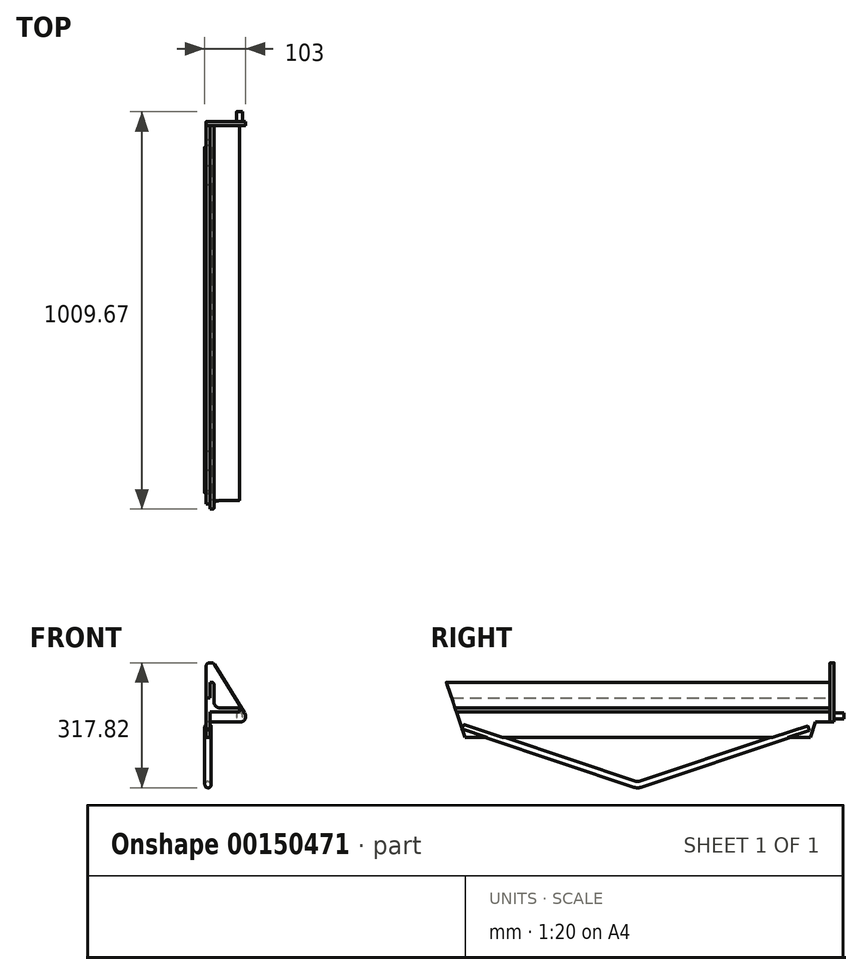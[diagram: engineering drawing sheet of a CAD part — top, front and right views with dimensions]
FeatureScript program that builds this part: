
annotation { "Feature Type Name" : "Feature", "Feature Type Description" : "" }
export const myFeature = defineFeature(function(context is Context, id is Id, definition is map)
    precondition{}
    {
        {
            var Q0;
            Q0=qCreatedBy(makeId("Front.planeOp"),FACE);
            var sketch = newSketch(context, id + "F0", { "sketchPlane" : qUnion([Q0])});
            skLineSegment(sketch, "E0", {"start": v(0, 75) * mm, "end": v(0, 0) * mm});
            skLineSegment(sketch, "E1", {"start": v(0, 0) * mm, "end": v(75, 0) * mm});
            skLineSegment(sketch, "E2", {"start": v(0, 75) * mm, "end": v(5, 75) * mm});
            skLineSegment(sketch, "E3", {"start": v(10, 70) * mm, "end": v(10, 26) * mm});
            skLineSegment(sketch, "E4", {"start": v(26, 10) * mm, "end": v(70, 10) * mm});
            skLineSegment(sketch, "E5", {"start": v(75, 5) * mm, "end": v(75, 0) * mm});
            skPoint(sketch, "E6.visualSharp", {"position": v(10, 10) * mm});
            skArc(sketch, "E6.filletArc", {"start": v(10, 26) * mm, "mid": v(14.69, 14.69) * mm, "end": v(26, 10) * mm});
            skPoint(sketch, "E7.visualSharp", {"position": v(10, 75) * mm});
            skArc(sketch, "E7.filletArc", {"start": v(10, 70) * mm, "mid": v(8.54, 73.54) * mm, "end": v(5, 75) * mm});
            skPoint(sketch, "E8.visualSharp", {"position": v(75, 10) * mm});
            skArc(sketch, "E8.filletArc", {"start": v(75, 5) * mm, "mid": v(73.54, 8.54) * mm, "end": v(70, 10) * mm});
            skSolve(sketch);
        }
        {
            var Q0;
            Q0=makeQuery(id+"F0.imprint","IMPRINT",FACE,{"disambiguationData":[TD([[makeQuery(id+"F0.imprint","IMPRINT",EDGE,{"derivedFrom":sQuery(id+"F0.wireOp",EDGE,"E0")}),1.0]])]});
            extrude(context, id + "F1", {"entities" : qUnion([Q0]), "depth" : 489 * mm, "hasSecondDirection" : true, "secondDirectionOppositeDirection" : true, "secondDirectionDepth" : 489 * mm});
        }
        {
            var Q0;
            Q0=qCreatedBy(makeId("Front.planeOp"),FACE);
            var sketch = newSketch(context, id + "F2", { "sketchPlane" : qUnion([Q0])});
            skLineSegment(sketch, "E9.bottom", {"start": v(0, 35) * mm, "end": v(-10, 35) * mm});
            skLineSegment(sketch, "E9.top", {"start": v(0, -65) * mm, "end": v(-10, -65) * mm});
            skLineSegment(sketch, "E9.left", {"start": v(0, 35) * mm, "end": v(0, -65) * mm});
            skLineSegment(sketch, "E9.right", {"start": v(-10, 35) * mm, "end": v(-10, -65) * mm});
            skSolve(sketch);
        }
        {
            var Q0;
            Q0=makeQuery(id+"F2.imprint","IMPRINT",FACE,{"disambiguationData":[TD([[makeQuery(id+"F2.imprint","IMPRINT",EDGE,{"derivedFrom":sQuery(id+"F2.wireOp",EDGE,"5NroJfMc-e3D6-tdf7-pEij-eTBKpccjXv2T.bottom")}),-1.0]])]});
            var Q1;
            Q1=makeQuery(id+"F2.imprint","IMPRINT",FACE,{"disambiguationData":[TD([[makeQuery(id+"F2.imprint","IMPRINT",EDGE,{"derivedFrom":sQuery(id+"F2.wireOp",EDGE,"E9.bottom")}),1.0]])]});
            extrude(context, id + "F3", {"entities" : qUnion([Q0, Q1]), "operationType" : NewBodyOperationType.ADD, "depth" : 489 * mm, "hasSecondDirection" : true, "secondDirectionOppositeDirection" : true, "secondDirectionDepth" : 489 * mm});
        }
        {
            var Q0;
            Q0=makeQuery(id+"F3.boolean.opBoolean","MERGE",FACE,{"derivedFrom":[makeQuery(id+"F1.opExtrude","CAP_FACE",FACE,{"disambiguationData":[OSD([sQuery(id+"F0.wireOp",EDGE,"E0"),sQuery(id+"F0.wireOp",EDGE,"E1"),sQuery(id+"F0.wireOp",EDGE,"E2"),sQuery(id+"F0.wireOp",EDGE,"E3"),sQuery(id+"F0.wireOp",EDGE,"E4"),sQuery(id+"F0.wireOp",EDGE,"E5"),sQuery(id+"F0.wireOp",EDGE,"E6.filletArc"),sQuery(id+"F0.wireOp",EDGE,"E7.filletArc"),sQuery(id+"F0.wireOp",EDGE,"E8.filletArc")])],"isStart":true}),makeQuery(id+"F3.opExtrude","CAP_FACE",FACE,{"disambiguationData":[OSD([sQuery(id+"F2.wireOp",EDGE,"5NroJfMc-e3D6-tdf7-pEij-eTBKpccjXv2T.bottom"),sQuery(id+"F2.wireOp",EDGE,"5NroJfMc-e3D6-tdf7-pEij-eTBKpccjXv2T.top"),sQuery(id+"F2.wireOp",EDGE,"5NroJfMc-e3D6-tdf7-pEij-eTBKpccjXv2T.left"),sQuery(id+"F2.wireOp",EDGE,"5NroJfMc-e3D6-tdf7-pEij-eTBKpccjXv2T.right")])],"isStart":true})]});
            var sketch = newSketch(context, id + "F4", { "sketchPlane" : qUnion([Q0])});
            skLineSegment(sketch, "E10.bottom", {"start": v(10, -25) * mm, "end": v(-90, -25) * mm});
            skLineSegment(sketch, "E10.top", {"start": v(10, 125) * mm, "end": v(-8.54, 125) * mm});
            skLineSegment(sketch, "E10.left", {"start": v(10, -25) * mm, "end": v(10, 125) * mm});
            skLineSegment(sketch, "E10.right", {"start": v(-90, -25) * mm, "end": v(-90, -5) * mm});
            skLineSegment(sketch, "E11", {"start": v(-8.54, 125) * mm, "end": v(-90, -5) * mm});
            skPoint(sketch, "E11.startSnap0", {"position": v(-8.54, 73.54) * mm});
            skSolve(sketch);
        }
        {
            var Q0;
            Q0 = qSketchRegion(id + "F4", true);
            extrude(context, id + "F5", {"entities" : qUnion([Q0]), "operationType" : NewBodyOperationType.ADD, "depth" : 10 * mm});
        }
        {
            var Q0;
            Q0=makeQuery(id+"F5.opExtrude","SWEPT_EDGE",EDGE,{"disambiguationData":[OSD([sQuery(id+"F4.wireOp",EDGE,"E10.top"),sQuery(id+"F4.wireOp",EDGE,"E11")])]});
            var Q1;
            Q1=makeQuery(id+"F5.opExtrude","SWEPT_EDGE",EDGE,{"disambiguationData":[OSD([sQuery(id+"F4.wireOp",EDGE,"E10.right"),sQuery(id+"F4.wireOp",EDGE,"E11")])]});
            var Q2;
            Q2=makeQuery(id+"F5.opExtrude","SWEPT_EDGE",EDGE,{"disambiguationData":[OSD([sQuery(id+"F4.wireOp",EDGE,"E10.bottom"),sQuery(id+"F4.wireOp",EDGE,"E10.right")])]});
            var Q3;
            Q3=makeQuery(id+"F5.opExtrude","SWEPT_EDGE",EDGE,{"disambiguationData":[OSD([sQuery(id+"F4.wireOp",EDGE,"E10.top"),sQuery(id+"F4.wireOp",EDGE,"E10.left")])]});
            fillet(context, id + "F6", {"entities" : qUnion([Q0, Q1, Q2, Q3]), "radius" : 10 * mm, "tangentPropagation" : true, "allowEdgeOverflow" : false});
        }
        {
            var Q0;
            Q0=makeQuery(id+"F5.opExtrude","CAP_FACE",FACE,{"disambiguationData":[OSD([sQuery(id+"F4.wireOp",EDGE,"E10.bottom"),sQuery(id+"F4.wireOp",EDGE,"E10.top"),sQuery(id+"F4.wireOp",EDGE,"E10.left"),sQuery(id+"F4.wireOp",EDGE,"E10.right"),sQuery(id+"F4.wireOp",EDGE,"E11")])],"isStart":false});
            var sketch = newSketch(context, id + "F7", { "sketchPlane" : qUnion([Q0])});
            skCircle(sketch, "E12", {"center": v(-75, -10) * mm, "radius": 8 * mm});
            skSolve(sketch);
        }
        {
            var Q0;
            Q0=makeQuery(id+"F7.imprint","IMPRINT",FACE,{"disambiguationData":[TD([[makeQuery(id+"F7.imprint","IMPRINT",EDGE,{"derivedFrom":sQuery(id+"F7.wireOp",EDGE,"E12")}),1.0]])]});
            extrude(context, id + "F8", {"entities" : qUnion([Q0]), "operationType" : NewBodyOperationType.ADD, "depth" : 25 * mm});
        }
        {
            var Q0;
            Q0=makeQuery(id+"F3.opExtrude","CAP_EDGE",EDGE,{"disambiguationData":[OSD([sQuery(id+"F2.wireOp",EDGE,"E9.top")])],"isStart":false});
            var Q1;
            Q1=makeQuery(id+"F3.opExtrude","CAP_EDGE",EDGE,{"disambiguationData":[OSD([sQuery(id+"F2.wireOp",EDGE,"E9.top")])],"isStart":true});
            chamfer(context, id + "F9", {"entities" : qUnion([Q0, Q1]), "chamferType" : ChamferType.TWO_OFFSETS, "width1" : 150 * mm, "oppositeDirection" : false, "width2" : 50 * mm, "tangentPropagation" : true});
        }
        {
            var Q0;
            {var subQ0=sQuery(id+"F4.wireOp",EDGE,"E10.left");Q0=makeQuery(id+"FGluRxbnb6SE4h9_1.1.F5.boolean.opBoolean","MERGE",FACE,{"derivedFrom":[makeQuery(id+"F5.boolean.opBoolean","MERGE",FACE,{"derivedFrom":[makeQuery(id+"F3.opExtrude","SWEPT_FACE",FACE,{"disambiguationData":[OSD([sQuery(id+"F2.wireOp",EDGE,"E9.right")])]}),makeQuery(id+"F5.opExtrude","SWEPT_FACE",FACE,{"disambiguationData":[OSD([subQ0])]})]}),makeQuery(id+"FGluRxbnb6SE4h9_1.1.F5.opExtrude","SWEPT_FACE",FACE,{"disambiguationData":[OSD([subQ0])]})]});}
            cPlane(context, id + "F10", {"entities" : qUnion([Q0]), "cplaneType" : CPlaneType.OFFSET, "offset" : 5 * mm, "oppositeDirection" : true, "width" : 150 * mm, "height" : 150 * mm});
        }
        {
            var Q0;
            Q0=qCreatedBy(id+"F10.planeOp",FACE);
            var sketch = newSketch(context, id + "F11", { "sketchPlane" : qUnion([Q0])});
            skLineSegment(sketch, "E13", {"start": v(444.1, -37.88) * mm, "end": v(6.32, -183.8) * mm});
            skLineSegment(sketch, "E14", {"start": v(-6.32, -183.8) * mm, "end": v(-434.51, -41.07) * mm});
            skPoint(sketch, "E15.visualSharp", {"position": v(0, -185.9) * mm});
            skArc(sketch, "E15.filletArc", {"start": v(-6.32, -183.8) * mm, "mid": v(0, -184.82) * mm, "end": v(6.32, -183.8) * mm});
            skSolve(sketch);
        }
        {
            var Q0;
            Q0=sQuery(id+"F11.wireOp",EDGE,"E14");
            var Q1;
            Q1=sQuery(id+"F11.wireOp",VERTEX,"E14.end");
            cPlane(context, id + "F12", {"entities" : qUnion([Q0, Q1]), "cplaneType" : CPlaneType.CURVE_POINT, "offset" : 25 * mm, "width" : 150 * mm, "height" : 150 * mm});
        }
        {
            var Q0;
            Q0=qCreatedBy(id+"F12.planeOp",FACE);
            var sketch = newSketch(context, id + "F13", { "sketchPlane" : qUnion([Q0])});
            skCircle(sketch, "E16", {"center": v(5, -176.37) * mm, "radius": 8 * mm});
            skSolve(sketch);
        }
        {
            var Q0;
            Q0=makeQuery(id+"F13.imprint","IMPRINT",FACE,{"disambiguationData":[TD([[makeQuery(id+"F13.imprint","IMPRINT",EDGE,{"derivedFrom":sQuery(id+"F13.wireOp",EDGE,"E16")}),1.0]])]});
            var Q1;
            Q1=sQuery(id+"F11.wireOp",EDGE,"E14");
            var Q2;
            Q2=sQuery(id+"F11.wireOp",EDGE,"E15.filletArc");
            var Q3;
            Q3=sQuery(id+"F11.wireOp",EDGE,"E13");
            sweep(context, id + "F14", {"operationType" : NewBodyOperationType.ADD, "profiles" : qUnion([Q0]), "path" : qUnion([Q1, Q2, Q3])});
        }
    });
